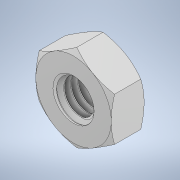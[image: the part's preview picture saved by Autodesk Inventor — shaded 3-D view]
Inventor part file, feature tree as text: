
AUTODESK INVENTOR PART (.ipt)
format: ipt  version: 2022 (Build 260153000, 153)  size: 250,880 bytes
history: mixed  units: in
note: dims shown in document units (in); Inventor stores cm internally (conversion verified against a paired STEP export)
features: mirror x1, imported_body x1
ambient origin geometry x8: Origin, YZ Plane, XZ Plane, XY Plane, X Axis, Y Axis, Z Axis, Center Point
bodies: Solid1 (imported_parasolid)
feature tree (2):
  mirror  "Mirror2"
  imported_body  NMx_Import_Brep_tag  [imported B-rep: ~6 faces, bbox_mm=None]
